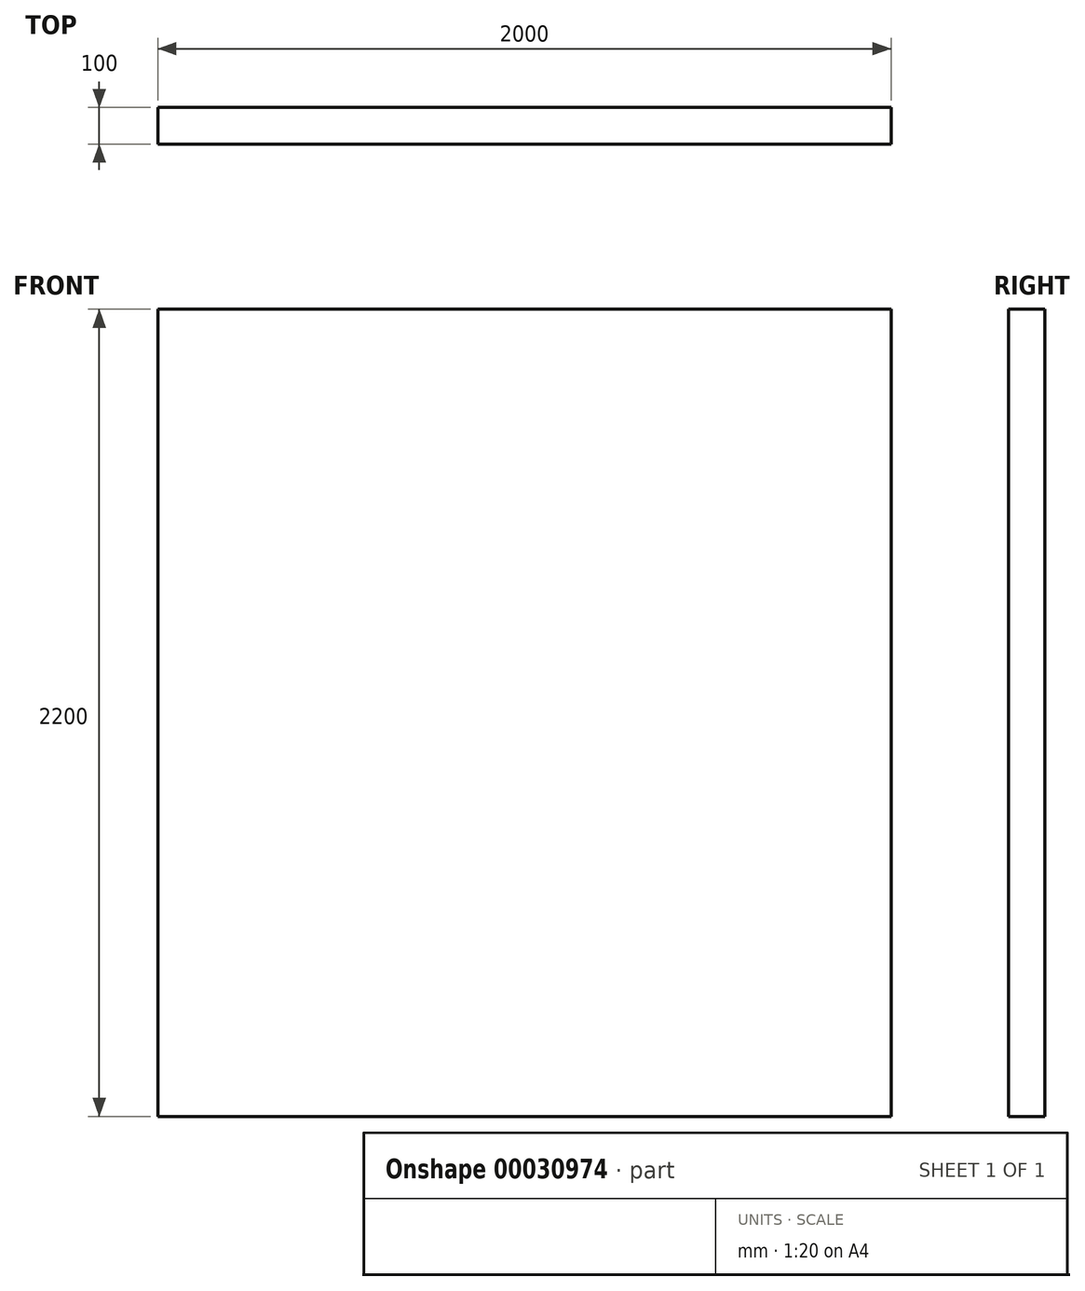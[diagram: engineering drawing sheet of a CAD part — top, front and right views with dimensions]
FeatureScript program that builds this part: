
annotation { "Feature Type Name" : "Feature", "Feature Type Description" : "" }
export const myFeature = defineFeature(function(context is Context, id is Id, definition is map)
    precondition{}
    {
        {
            var Q0;
            Q0=qCreatedBy(makeId("Front.planeOp"),FACE);
            var sketch = newSketch(context, id + "F0", { "sketchPlane" : qUnion([Q0])});
            skLineSegment(sketch, "E0.rect.bottom", {"start": v(-1000, 1100) * mm, "end": v(1000, 1100) * mm});
            skLineSegment(sketch, "E0.rect.top", {"start": v(-1000, -1100) * mm, "end": v(1000, -1100) * mm});
            skLineSegment(sketch, "E0.rect.left", {"start": v(-1000, 1100) * mm, "end": v(-1000, -1100) * mm});
            skLineSegment(sketch, "E0.rect.right", {"start": v(1000, 1100) * mm, "end": v(1000, -1100) * mm});
            skPoint(sketch, "E0.rect.middle", {"position": v(0, 0) * mm});
            skSolve(sketch);
        }
        {
            var Q0;
            Q0=makeQuery(id+"F0.imprint","IMPRINT",FACE,{"disambiguationData":[TD([[makeQuery(id+"F0.imprint","IMPRINT",EDGE,{"derivedFrom":sQuery(id+"F0.wireOp",EDGE,"E0.rect.bottom")}),-1.0]])]});
            extrude(context, id + "F1", {"entities" : qUnion([Q0]), "depth" : 100 * mm});
        }
    });
